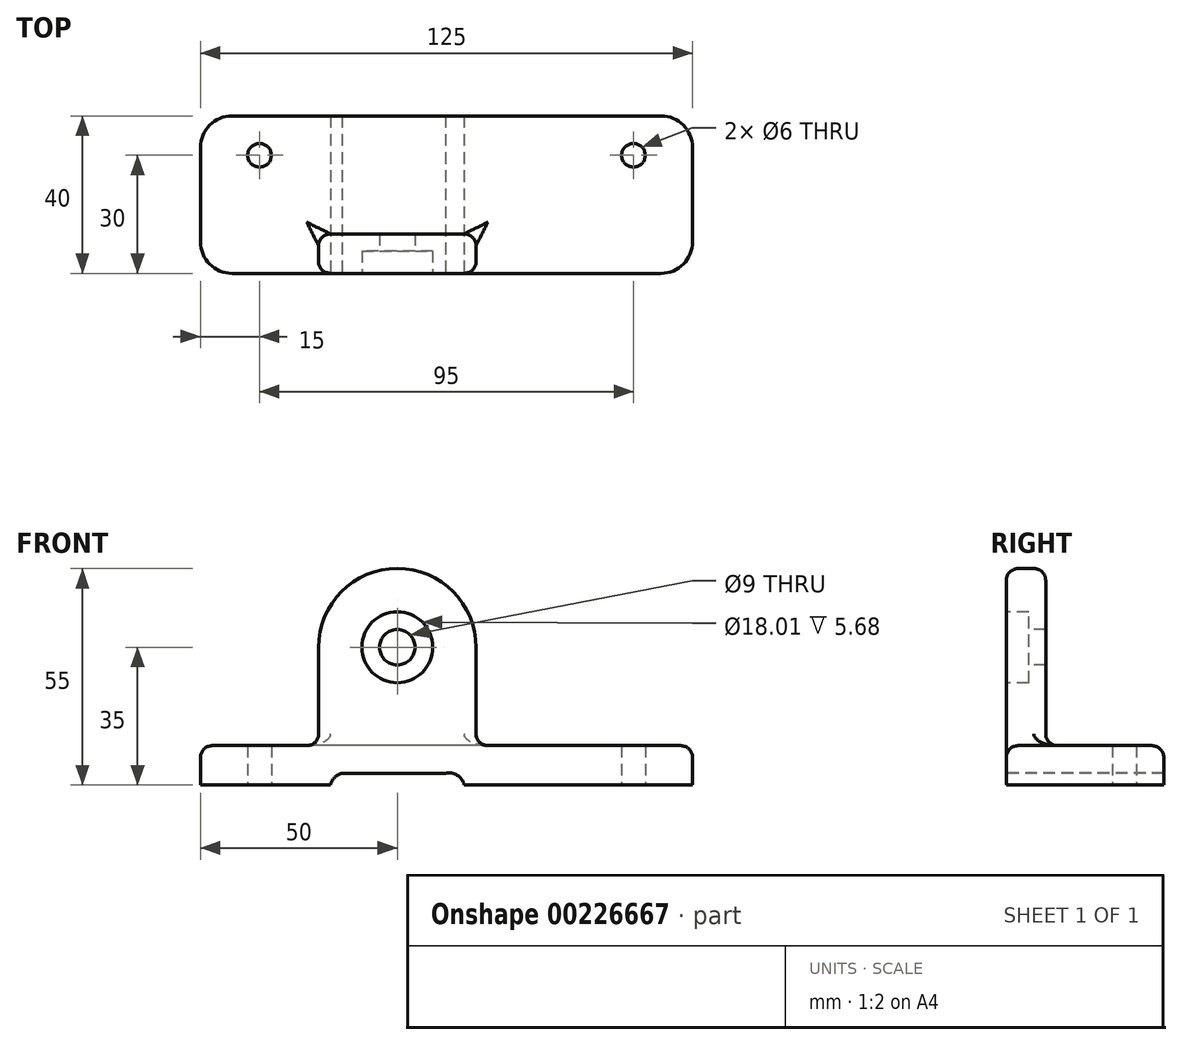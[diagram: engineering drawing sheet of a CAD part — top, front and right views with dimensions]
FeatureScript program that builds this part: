
annotation { "Feature Type Name" : "Feature", "Feature Type Description" : "" }
export const myFeature = defineFeature(function(context is Context, id is Id, definition is map)
    precondition{}
    {
        {
            var Q0;
            Q0=qCreatedBy(makeId("Top.planeOp"),FACE);
            var sketch = newSketch(context, id + "F0", { "sketchPlane" : qUnion([Q0])});
            skLineSegment(sketch, "E0.bottom", {"start": v(62.5, 20) * mm, "end": v(-62.5, 20) * mm});
            skLineSegment(sketch, "E0.top", {"start": v(62.5, -20) * mm, "end": v(-62.5, -20) * mm});
            skLineSegment(sketch, "E0.left", {"start": v(62.5, 20) * mm, "end": v(62.5, -20) * mm});
            skLineSegment(sketch, "E0.right", {"start": v(-62.5, 20) * mm, "end": v(-62.5, -20) * mm});
            skPoint(sketch, "E0.middle", {"position": v(0, 0) * mm});
            skSolve(sketch);
        }
        {
            var Q0;
            Q0 = qSketchRegion(id + "F0", true);
            extrude(context, id + "F1", {"entities" : qUnion([Q0]), "depth" : 10 * mm});
        }
        {
            var Q0;
            Q0=makeQuery(id+"F1.opExtrude","SWEPT_FACE",FACE,{"disambiguationData":[OSD([sQuery(id+"F0.wireOp",EDGE,"E0.top")])]});
            var sketch = newSketch(context, id + "F2", { "sketchPlane" : qUnion([Q0])});
            skArc(sketch, "E1", {"start": v(7.5, 35) * mm, "mid": v(-12.5, 55) * mm, "end": v(-32.5, 35) * mm});
            skLineSegment(sketch, "E2", {"start": v(-32.5, 35) * mm, "end": v(-32.5, 13) * mm});
            skLineSegment(sketch, "E3", {"start": v(7.5, 35) * mm, "end": v(7.5, 13) * mm});
            skArc(sketch, "E4", {"start": v(-35.5, 10) * mm, "mid": v(-33.38, 10.88) * mm, "end": v(-32.5, 13) * mm});
            skArc(sketch, "E5", {"start": v(7.5, 13) * mm, "mid": v(8.38, 10.88) * mm, "end": v(10.5, 10) * mm});
            skPoint(sketch, "E6.orphan", {"position": v(-12.5, 10) * mm});
            skSolve(sketch);
        }
        {
            var Q0;
            Q0 = qSketchRegion(id + "F2", true);
            var Q1;
            Q1=makeQuery(id+"F2.imprint","IMPRINT",FACE,{"disambiguationData":[TD([[makeQuery(id+"F2.imprint","IMPRINT",EDGE,{"derivedFrom":sQuery(id+"F2.wireOp",EDGE,"E1")}),1.0]])]});
            extrude(context, id + "F3", {"entities" : qUnion([Q0, Q1]), "operationType" : NewBodyOperationType.ADD, "oppositeDirection" : true, "depth" : 13 * mm});
        }
        {
            var Q0;
            Q0=makeQuery(id+"F1.opExtrude","SWEPT_FACE",FACE,{"disambiguationData":[OSD([sQuery(id+"F0.wireOp",EDGE,"E0.left")])]});
            var sketch = newSketch(context, id + "F4", { "sketchPlane" : qUnion([Q0])});
            skLineSegment(sketch, "E7", {"start": v(-10, 13) * mm, "end": v(-10, 62.98) * mm});
            skLineSegment(sketch, "E8", {"start": v(-10, 62.98) * mm, "end": v(-7, 62.98) * mm});
            skLineSegment(sketch, "E9", {"start": v(-7, 10) * mm, "end": v(-7, 13) * mm});
            skArc(sketch, "E10", {"start": v(-10, 13) * mm, "mid": v(-9.12, 10.88) * mm, "end": v(-7, 10) * mm});
            skLineSegment(sketch, "E11", {"start": v(-7, 13) * mm, "end": v(-7, 62.98) * mm});
            skSolve(sketch);
        }
        {
            var Q0;
            Q0 = qSketchRegion(id + "F4", true);
            extrude(context, id + "F5", {"entities" : qUnion([Q0]), "operationType" : NewBodyOperationType.REMOVE, "endBound" : BoundingType.THROUGH_ALL, "oppositeDirection" : true, "depth" : 25 * mm});
        }
        {
            var Q0;
            Q0=makeQuery(id+"F1.opExtrude","SWEPT_EDGE",EDGE,{"disambiguationData":[OSD([sQuery(id+"F0.wireOp",EDGE,"E0.top"),sQuery(id+"F0.wireOp",EDGE,"E0.left")])]});
            var Q1;
            Q1=makeQuery(id+"F1.opExtrude","SWEPT_EDGE",EDGE,{"disambiguationData":[OSD([sQuery(id+"F0.wireOp",EDGE,"E0.bottom"),sQuery(id+"F0.wireOp",EDGE,"E0.left")])]});
            var Q2;
            Q2=makeQuery(id+"F1.opExtrude","SWEPT_EDGE",EDGE,{"disambiguationData":[OSD([sQuery(id+"F0.wireOp",EDGE,"E0.top"),sQuery(id+"F0.wireOp",EDGE,"E0.right")])]});
            var Q3;
            Q3=makeQuery(id+"F1.opExtrude","SWEPT_EDGE",EDGE,{"disambiguationData":[OSD([sQuery(id+"F0.wireOp",EDGE,"E0.bottom"),sQuery(id+"F0.wireOp",EDGE,"E0.right")])]});
            fillet(context, id + "F6", {"entities" : qUnion([Q0, Q1, Q2, Q3]), "radius" : 8 * mm, "tangentPropagation" : true, "allowEdgeOverflow" : false});
        }
        {
            var Q0;
            Q0=makeQuery(id+"F3.opExtrude","CAP_EDGE",EDGE,{"disambiguationData":[OSD([sQuery(id+"F2.wireOp",EDGE,"E1")])],"isStart":true});
            var Q1;
            Q1=makeQuery(id+"F5.boolean.opBoolean","INTERSECT",EDGE,{"derivedFrom":[makeQuery(id+"F3.opExtrude","SWEPT_FACE",FACE,{"disambiguationData":[OSD([sQuery(id+"F2.wireOp",EDGE,"E1")])]}),makeQuery(id+"F5.opExtrude","SWEPT_FACE",FACE,{"disambiguationData":[OSD([sQuery(id+"F4.wireOp",EDGE,"E7")])]})]});
            fillet(context, id + "F7", {"entities" : qUnion([Q0, Q1]), "radius" : 3 * mm, "tangentPropagation" : true, "allowEdgeOverflow" : false});
        }
        {
            var Q0;
            Q0=makeQuery(id+"F1.opExtrude","CAP_FACE",FACE,{"disambiguationData":[OSD([sQuery(id+"F0.wireOp",EDGE,"E0.bottom"),sQuery(id+"F0.wireOp",EDGE,"E0.top"),sQuery(id+"F0.wireOp",EDGE,"E0.left"),sQuery(id+"F0.wireOp",EDGE,"E0.right")])],"isStart":true});
            var sketch = newSketch(context, id + "F8", { "sketchPlane" : qUnion([Q0])});
            skCircle(sketch, "E12", {"center": v(-47.5, -10) * mm, "radius": 3 * mm});
            skCircle(sketch, "E13", {"center": v(47.5, -10) * mm, "radius": 3 * mm});
            skSolve(sketch);
        }
        {
            var Q0;
            Q0=makeQuery(id+"F8.imprint","IMPRINT",FACE,{"disambiguationData":[TD([[makeQuery(id+"F8.imprint","IMPRINT",EDGE,{"derivedFrom":sQuery(id+"F8.wireOp",EDGE,"E13")}),1.0]])]});
            var Q1;
            Q1=makeQuery(id+"F8.imprint","IMPRINT",FACE,{"disambiguationData":[TD([[makeQuery(id+"F8.imprint","IMPRINT",EDGE,{"derivedFrom":sQuery(id+"F8.wireOp",EDGE,"E12")}),1.0]])]});
            extrude(context, id + "F9", {"entities" : qUnion([Q0, Q1]), "operationType" : NewBodyOperationType.REMOVE, "endBound" : BoundingType.THROUGH_ALL, "oppositeDirection" : true, "depth" : 25 * mm});
        }
        {
            var Q0;
            {var subQ0=sQuery(id+"F0.wireOp",EDGE,"E0.top");Q0=makeQuery(id+"F3.boolean.opBoolean","MERGE",FACE,{"derivedFrom":[makeQuery(id+"F1.opExtrude","SWEPT_FACE",FACE,{"disambiguationData":[OSD([subQ0])]}),makeQuery(id+"F3.opExtrude","CAP_FACE",FACE,{"disambiguationData":[OSD([subQ0,sQuery(id+"F2.wireOp",EDGE,"E1"),sQuery(id+"F2.wireOp",EDGE,"E2"),sQuery(id+"F2.wireOp",EDGE,"E3"),sQuery(id+"F2.wireOp",EDGE,"E4"),sQuery(id+"F2.wireOp",EDGE,"E5")])],"isStart":true})]});}
            var sketch = newSketch(context, id + "F10", { "sketchPlane" : qUnion([Q0])});
            skLineSegment(sketch, "E14", {"start": v(1.5, 3) * mm, "end": v(-26.5, 3) * mm});
            skArc(sketch, "E15", {"start": v(-26.5, 3) * mm, "mid": v(-28.43, 1.93) * mm, "end": v(-29.5, 0) * mm});
            skPoint(sketch, "E15.third.point", {"position": v(-27.97, -4.13) * mm});
            skArc(sketch, "E16", {"start": v(4.5, 0) * mm, "mid": v(2.72, 2.5) * mm, "end": v(-0.3, 3) * mm});
            skPoint(sketch, "E16.third.point", {"position": v(4.38, -2.2) * mm});
            skPoint(sketch, "E17.end.orphan", {"position": v(-26.5, 3) * mm});
            skPoint(sketch, "E18.start.orphan", {"position": v(-29.5, 3) * mm});
            skPoint(sketch, "E19.end.orphan", {"position": v(1.5, 3) * mm});
            skPoint(sketch, "E20.end.orphan", {"position": v(4.5, 3) * mm});
            skPoint(sketch, "E21.start.orphan", {"position": v(-12.5, 52) * mm});
            skPoint(sketch, "E22.start.orphan", {"position": v(-12.5, 0) * mm});
            skLineSegment(sketch, "E23", {"start": v(-29.5, 0) * mm, "end": v(4.5, 0) * mm});
            skSolve(sketch);
        }
        {
            var Q0;
            Q0 = qSketchRegion(id + "F10", true);
            extrude(context, id + "F11", {"entities" : qUnion([Q0]), "operationType" : NewBodyOperationType.REMOVE, "endBound" : BoundingType.THROUGH_ALL, "oppositeDirection" : true, "depth" : 25 * mm});
        }
        {
            var Q0;
            {var subQ0=sQuery(id+"F0.wireOp",EDGE,"E0.top");Q0=makeQuery(id+"F3.boolean.opBoolean","MERGE",FACE,{"derivedFrom":[makeQuery(id+"F1.opExtrude","SWEPT_FACE",FACE,{"disambiguationData":[OSD([subQ0])]}),makeQuery(id+"F3.opExtrude","CAP_FACE",FACE,{"disambiguationData":[OSD([subQ0,sQuery(id+"F2.wireOp",EDGE,"E1"),sQuery(id+"F2.wireOp",EDGE,"E2"),sQuery(id+"F2.wireOp",EDGE,"E3"),sQuery(id+"F2.wireOp",EDGE,"E4"),sQuery(id+"F2.wireOp",EDGE,"E5")])],"isStart":true})]});}
            var sketch = newSketch(context, id + "F12", { "sketchPlane" : qUnion([Q0])});
            skCircle(sketch, "E24", {"center": v(-12.5, 35) * mm, "radius": 4.5 * mm});
            skCircle(sketch, "E25", {"center": v(-12.5, 35) * mm, "radius": 9 * mm});
            skPoint(sketch, "E26.start.orphan", {"position": v(-12.5, 52) * mm});
            skPoint(sketch, "E27.start.orphan", {"position": v(-29.5, 35) * mm});
            skPoint(sketch, "E28.orphan", {"position": v(4.5, 35) * mm});
            skSolve(sketch);
        }
        {
            var Q0;
            Q0=makeQuery(id+"F12.imprint","IMPRINT",FACE,{"disambiguationData":[TD([[makeQuery(id+"F12.imprint","IMPRINT",EDGE,{"derivedFrom":sQuery(id+"F12.wireOp",EDGE,"E24")}),1.0]])]});
            extrude(context, id + "F13", {"entities" : qUnion([Q0]), "operationType" : NewBodyOperationType.REMOVE, "endBound" : BoundingType.THROUGH_ALL, "oppositeDirection" : true, "depth" : 25 * mm});
        }
        {
            var Q0;
            Q0 = qSketchRegion(id + "F12", true);
            extrude(context, id + "F14", {"entities" : qUnion([Q0]), "operationType" : NewBodyOperationType.REMOVE, "oppositeDirection" : true, "depth" : 5.68 * mm});
        }
    });
